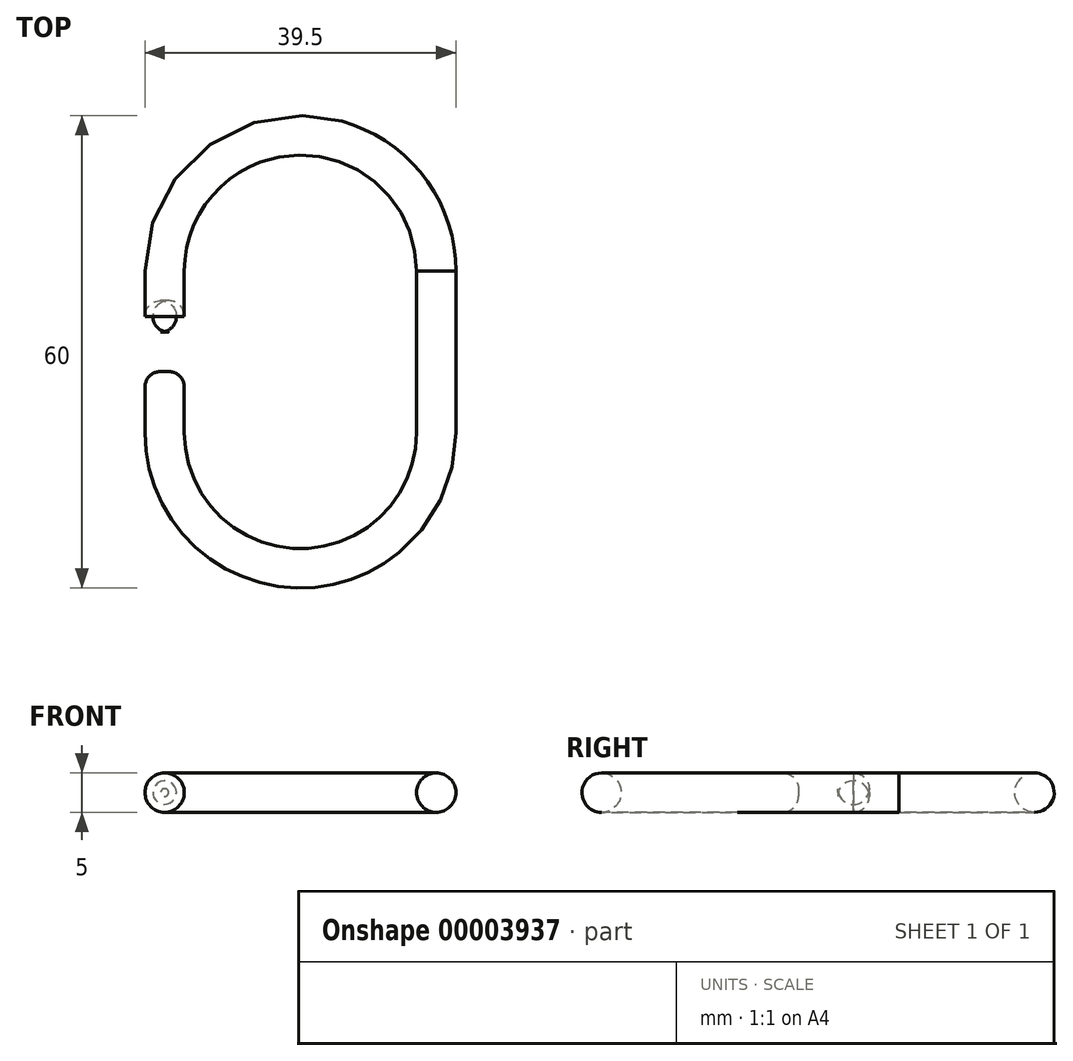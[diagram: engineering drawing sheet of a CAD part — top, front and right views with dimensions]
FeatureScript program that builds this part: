
annotation { "Feature Type Name" : "Feature", "Feature Type Description" : "" }
export const myFeature = defineFeature(function(context is Context, id is Id, definition is map)
    precondition{}
    {
        {
            var Q0;
            Q0=qCreatedBy(makeId("Top.planeOp"),FACE);
            var sketch = newSketch(context, id + "F0", { "sketchPlane" : qUnion([Q0])});
            skLineSegment(sketch, "E0", {"start": v(17.25, 0) * mm, "end": v(17.25, -20.5) * mm});
            skArc(sketch, "E1", {"start": v(17.25, 0) * mm, "mid": v(0, 17.25) * mm, "end": v(-17.25, 0) * mm});
            skArc(sketch, "E2", {"start": v(17.25, -20.5) * mm, "mid": v(0, -37.75) * mm, "end": v(-17.25, -20.5) * mm});
            skLineSegment(sketch, "E3", {"start": v(-17.25, 0) * mm, "end": v(-17.25, -7.75) * mm});
            skLineSegment(sketch, "E4", {"start": v(-17.25, -12.75) * mm, "end": v(-17.25, -20.5) * mm});
            skSolve(sketch);
        }
        {
            var Q0;
            Q0=qCreatedBy(makeId("Front.planeOp"),FACE);
            var sketch = newSketch(context, id + "F1", { "sketchPlane" : qUnion([Q0])});
            skCircle(sketch, "E5", {"center": v(17.25, 0) * mm, "radius": 2.5 * mm});
            skSolve(sketch);
        }
        {
            var Q0;
            Q0=makeQuery(id+"F1.imprint","IMPRINT",FACE,{"disambiguationData":[TD([[makeQuery(id+"F1.imprint","IMPRINT",EDGE,{"derivedFrom":sQuery(id+"F1.wireOp",EDGE,"E5")}),1.0]])]});
            var Q1;
            Q1=sQuery(id+"F0.wireOp",EDGE,"E1");
            var Q2;
            Q2=sQuery(id+"F0.wireOp",EDGE,"E3");
            sweep(context, id + "F2", {"profiles" : qUnion([Q0]), "path" : qUnion([Q1, Q2])});
        }
        {
            var Q0;
            Q0=makeQuery(id+"F2.opSweep","CAP_FACE",FACE,{"disambiguationData":[OSD([sQuery(id+"F0.wireOp",VERTEX,"E1.start"),sQuery(id+"F1.wireOp",EDGE,"E5")])],"isStart":true});
            var Q1;
            Q1=sQuery(id+"F0.wireOp",EDGE,"E0");
            var Q2;
            Q2=sQuery(id+"F0.wireOp",EDGE,"E2");
            var Q3;
            Q3=sQuery(id+"F0.wireOp",EDGE,"E4");
            sweep(context, id + "F3", {"profiles" : qUnion([Q0]), "path" : qUnion([Q1, Q2, Q3])});
        }
        {
            var Q0;
            Q0=makeQuery(id+"F2.opSweep","CAP_EDGE",EDGE,{"disambiguationData":[OSD([sQuery(id+"F0.wireOp",VERTEX,"E3.end"),sQuery(id+"F1.wireOp",EDGE,"E5")])],"isStart":false});
            fillet(context, id + "F4", {"entities" : qUnion([Q0]), "radius" : 2 * mm, "tangentPropagation" : true, "allowEdgeOverflow" : false});
        }
        {
            var Q0;
            Q0=makeQuery(id+"F3.opSweep","CAP_EDGE",EDGE,{"disambiguationData":[OSD([sQuery(id+"F0.wireOp",VERTEX,"E1.start"),sQuery(id+"F0.wireOp",VERTEX,"E4.start"),sQuery(id+"F1.wireOp",EDGE,"E5")])],"isStart":false});
            fillet(context, id + "F5", {"entities" : qUnion([Q0]), "radius" : 2 * mm, "tangentPropagation" : true, "allowEdgeOverflow" : false});
        }
    });
